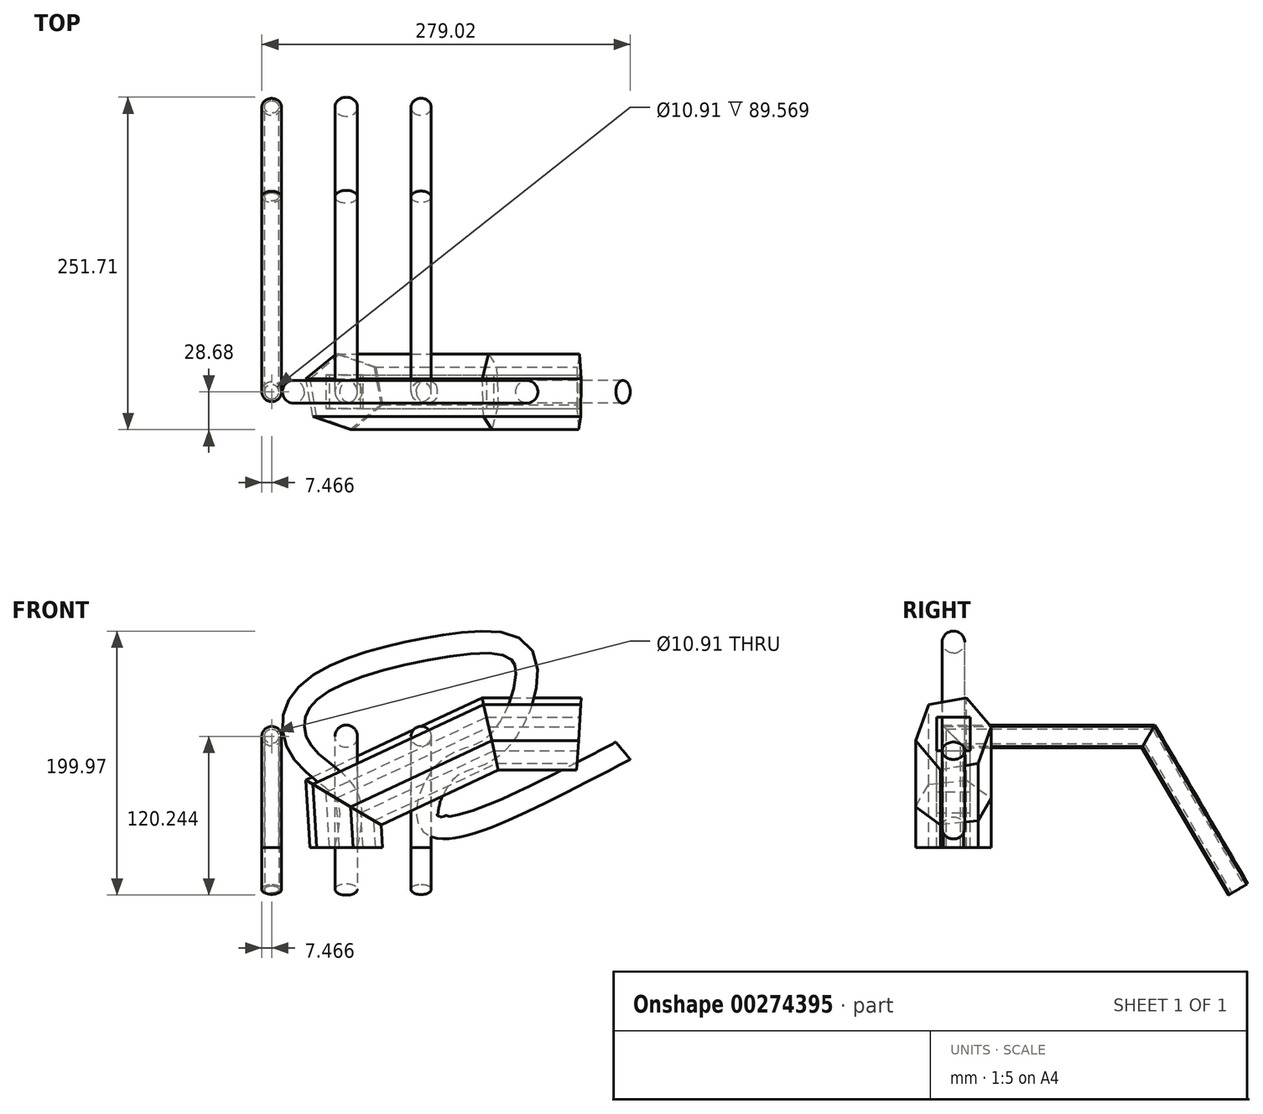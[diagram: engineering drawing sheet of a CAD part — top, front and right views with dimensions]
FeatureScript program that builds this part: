
annotation { "Feature Type Name" : "Feature", "Feature Type Description" : "" }
export const myFeature = defineFeature(function(context is Context, id is Id, definition is map)
    precondition{}
    {
        {
            var Q0;
            Q0=qCreatedBy(makeId("Top.planeOp"),FACE);
            var sketch = newSketch(context, id + "F0", { "sketchPlane" : qUnion([Q0])});
            skLineSegment(sketch, "E0.bottom", {"start": v(12.7, -12.7) * mm, "end": v(-12.7, -12.7) * mm});
            skLineSegment(sketch, "E0.top", {"start": v(12.7, 12.7) * mm, "end": v(-12.7, 12.7) * mm});
            skLineSegment(sketch, "E0.left", {"start": v(12.7, -12.7) * mm, "end": v(12.7, 12.7) * mm});
            skLineSegment(sketch, "E0.right", {"start": v(-12.7, -12.7) * mm, "end": v(-12.7, 12.7) * mm});
            skPoint(sketch, "E0.middle", {"position": v(0, 0) * mm});
            skCircle(sketch, "E1", {"center": v(0, 0) * mm, "radius": 8.55 * mm});
            skCircle(sketch, "E2.cCircle", {"center": v(0, 0) * mm, "radius": 25.24 * mm, "construction": true});
            skLineSegment(sketch, "E2.0", {"start": v(22.25, 18.83) * mm, "end": v(27.43, -9.85) * mm});
            skLineSegment(sketch, "E2.1", {"start": v(27.43, -9.85) * mm, "end": v(5.18, -28.68) * mm});
            skLineSegment(sketch, "E2.2", {"start": v(5.18, -28.68) * mm, "end": v(-22.25, -18.83) * mm});
            skLineSegment(sketch, "E2.3", {"start": v(-22.25, -18.83) * mm, "end": v(-27.43, 9.85) * mm});
            skLineSegment(sketch, "E2.4", {"start": v(-27.43, 9.85) * mm, "end": v(-5.18, 28.68) * mm});
            skLineSegment(sketch, "E2.5", {"start": v(-5.18, 28.68) * mm, "end": v(22.25, 18.83) * mm});
            skPoint(sketch, "E2.0.midPoint", {"position": v(24.84, 4.5) * mm});
            skCircle(sketch, "E3", {"center": v(-56.46, 0) * mm, "radius": 7.47 * mm});
            skPoint(sketch, "E3.centerSnap0", {"position": v(12.7, 0) * mm});
            skCircle(sketch, "E4", {"center": v(56.68, 0) * mm, "radius": 7.6 * mm});
            skCircle(sketch, "E5", {"center": v(-56.46, 0) * mm, "radius": 5.45 * mm});
            skSolve(sketch);
        }
        {
            var Q0;
            Q0=qCreatedBy(makeId("Front.planeOp"),FACE);
            var sketch = newSketch(context, id + "F1", { "sketchPlane" : qUnion([Q0])});
            skFitSpline(sketch, "E6", {"points": [v(0, 0) * mm, v(0, 39.96) * mm, v(-33.13, 71.96) * mm, v(-33.64, 111.66) * mm, v(64.18, 150.77) * mm, v(134.57, 143.14) * mm, v(112.32, 77.2) * mm, v(76.6, 58.6) * mm, v(63.66, 18.64) * mm, v(209.62, 73.2) * mm], "startDerivative": vector(105.52, 493.43) * mm, "endDerivative": vector(1153.04, 605.96) * mm});
            skSolve(sketch);
        }
        {
            var Q0;
            Q0=makeQuery(id+"F0.imprint","IMPRINT",FACE,{"disambiguationData":[TD([[makeQuery(id+"F0.imprint","IMPRINT",EDGE,{"derivedFrom":sQuery(id+"F0.wireOp",EDGE,"E1")}),1.0]])]});
            var Q1;
            Q1=sQuery(id+"F1.wireOp",EDGE,"E6");
            sweep(context, id + "F2", {"profiles" : qUnion([Q0]), "path" : qUnion([Q1])});
        }
        {
            var Q0;
            Q0=qCreatedBy(makeId("Front.planeOp"),FACE);
            var sketch = newSketch(context, id + "F3", { "sketchPlane" : qUnion([Q0])});
            skLineSegment(sketch, "E7", {"start": v(-103.1, 0) * mm, "end": v(-109.18, 97.52) * mm});
            skLineSegment(sketch, "E8", {"start": v(-109.18, 97.52) * mm, "end": v(86.17, 188.88) * mm});
            skLineSegment(sketch, "E9", {"start": v(86.17, 188.88) * mm, "end": v(182.7, 188.88) * mm});
            skSolve(sketch);
        }
        {
            var Q0;
            Q0=qCreatedBy(makeId("Right.planeOp"),FACE);
            var sketch = newSketch(context, id + "F4", { "sketchPlane" : qUnion([Q0])});
            skLineSegment(sketch, "E10", {"start": v(-62.82, 0) * mm, "end": v(-62.82, 146.94) * mm});
            skLineSegment(sketch, "E11", {"start": v(-62.82, 146.94) * mm, "end": v(183.58, 146.94) * mm});
            skLineSegment(sketch, "E12", {"start": v(183.58, 146.94) * mm, "end": v(269.84, 0) * mm});
            skSolve(sketch);
        }
        {
            var Q0;
            Q0=makeQuery(id+"F0.imprint","IMPRINT",FACE,{"disambiguationData":[TD([[makeQuery(id+"F0.imprint","IMPRINT",EDGE,{"derivedFrom":sQuery(id+"F0.wireOp",EDGE,"E1")}),1.0]])]});
            var Q1;
            Q1=makeQuery(id+"F0.imprint","IMPRINT",FACE,{"disambiguationData":[TD([[makeQuery(id+"F0.imprint","IMPRINT",EDGE,{"derivedFrom":sQuery(id+"F0.wireOp",EDGE,"E4")}),1.0]])]});
            var Q2;
            Q2=makeQuery(id+"F0.imprint","IMPRINT",FACE,{"disambiguationData":[TD([[makeQuery(id+"F0.imprint","IMPRINT",EDGE,{"derivedFrom":sQuery(id+"F0.wireOp",EDGE,"E3")}),1.0]])]});
            var Q3;
            Q3=sQuery(id+"F4.wireOp",EDGE,"E10");
            var Q4;
            Q4=sQuery(id+"F4.wireOp",EDGE,"E11");
            var Q5;
            Q5=sQuery(id+"F4.wireOp",EDGE,"E12");
            sweep(context, id + "F5", {"profiles" : qUnion([Q0, Q1, Q2]), "path" : qUnion([Q3, Q4, Q5])});
        }
        {
            var Q0;
            Q0=makeQuery(id+"F0.imprint","IMPRINT",FACE,{"disambiguationData":[TD([[makeQuery(id+"F0.imprint","IMPRINT",EDGE,{"derivedFrom":sQuery(id+"F0.wireOp",EDGE,"E0.bottom")}),1.0]])]});
            var Q1;
            Q1=sQuery(id+"F3.wireOp",EDGE,"E7");
            var Q2;
            Q2=sQuery(id+"F3.wireOp",EDGE,"E8");
            var Q3;
            Q3=sQuery(id+"F3.wireOp",EDGE,"E9");
            sweep(context, id + "F6", {"profiles" : qUnion([Q0]), "path" : qUnion([Q1, Q2, Q3])});
        }
    });
